# Revit family: O14621001_Lavamanos Ravenna Vessel Blanco
name_source: partatom
category: Plumbing Fixtures
units: mm (PartAtom-declared; Revit-internal decimal feet)

## family parameters
Always vertical = Yes
Cut with Voids When Loaded = No
OmniClass Number = 23.31.13.11
OmniClass Title = Single Sinks
Part Type = Normal
Room Calculation Point = No
Round Connector Dimension = Use Diameter
Shared = No
Work Plane-Based = No

## types (2) — shared parameters
Acabado = Brillante
Alto = 15 cm
Ancho = 40 cm
Colección = Lavamanos 2007
Creado por = IDD
Description = Nuestro lavamanos para sobreponer tipo Vessel es de práctico tamaño porque además se recomienda instalar con griferías a la pared o de mesón altas. ¡Lo mejor para tu espacio!
Dimensión del pozo = 39
Diámetro del desagüe = 44 mm
Fecha de creación = 10/08/2020
Forma = Ovalado
Garantía = Garantía completa para siempre en la porcelana
Largo = 33 cm
Línea = Ravenna
Materiales = Porcelana sanitaria
No incluye = Grifería
Productos compatibles = Grifería monocontrol alta, Grifería monocontrol a pared
Profundidad del pozo = 13 cm
Resistencia = Alta resistencia al rayado y cambios de temperatura
Tecnologías = CoverGloss, Aquaflow
Tipo de desagüe = Expuesto
Tipo de instalación = A pared
Tipo de lavamanos = Vessel
URL = https://corona.co
Uso = Residencial

## per-type parameters (varying)
| type | Material |
| Porcelana_sanitaria_blanca | Corona_Porcelana_Sanitaria_Blanco |
| Porcelana_sanitaria_hueso | Corona_Porcelana_Sanitaria_Hueso |

## geometry (parser evidence)
native form markers: Sweep x4
no freeform markers — native parametric forms only
